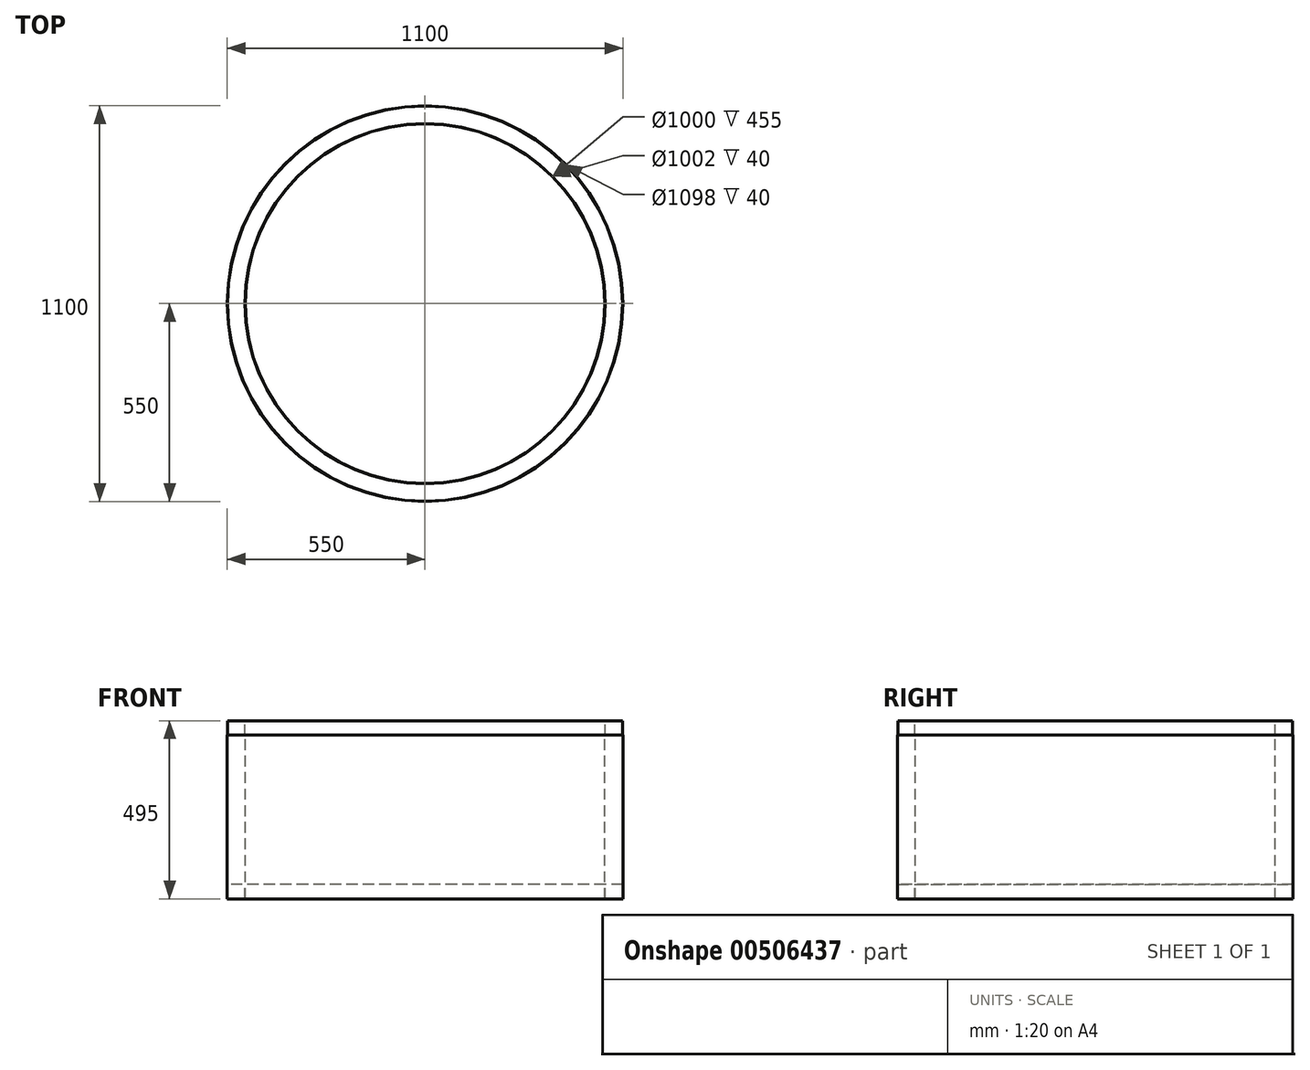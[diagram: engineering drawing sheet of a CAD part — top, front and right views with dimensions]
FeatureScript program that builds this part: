
annotation { "Feature Type Name" : "Feature", "Feature Type Description" : "" }
export const myFeature = defineFeature(function(context is Context, id is Id, definition is map)
    precondition{}
    {
        {
            var Q0;
            Q0=qCreatedBy(makeId("Front.planeOp"),FACE);
            var sketch = newSketch(context, id + "F0", { "sketchPlane" : qUnion([Q0])});
            skLineSegment(sketch, "E0", {"start": v(0, 150.29) * mm, "end": v(0, 1.7) * mm, "construction": true});
            skLineSegment(sketch, "E1", {"start": v(0, 450.26) * mm, "end": v(0, -453.52) * mm, "construction": true});
            skLineSegment(sketch, "E2", {"start": v(-500, -414.33) * mm, "end": v(-500, 40.67) * mm});
            skLineSegment(sketch, "E3", {"start": v(-500, 40.67) * mm, "end": v(-501, 40.67) * mm});
            skLineSegment(sketch, "E4", {"start": v(-501, 40.67) * mm, "end": v(-501, 80.67) * mm});
            skLineSegment(sketch, "E5", {"start": v(-501, 80.67) * mm, "end": v(-549, 80.67) * mm});
            skLineSegment(sketch, "E6", {"start": v(-549, 80.67) * mm, "end": v(-549, 40.67) * mm});
            skLineSegment(sketch, "E7", {"start": v(-549, 40.67) * mm, "end": v(-550, 40.67) * mm});
            skLineSegment(sketch, "E8", {"start": v(-550, 40.67) * mm, "end": v(-550, -414.33) * mm});
            skLineSegment(sketch, "E9", {"start": v(-550, -414.33) * mm, "end": v(-549, -414.33) * mm});
            skLineSegment(sketch, "E10", {"start": v(-549, -414.33) * mm, "end": v(-549, -374.33) * mm});
            skLineSegment(sketch, "E11", {"start": v(-549, -374.33) * mm, "end": v(-501, -374.33) * mm});
            skLineSegment(sketch, "E12", {"start": v(-501, -374.33) * mm, "end": v(-501, -414.33) * mm});
            skLineSegment(sketch, "E13", {"start": v(-501, -414.33) * mm, "end": v(-500, -414.33) * mm});
            skSolve(sketch);
        }
        {
            var Q0;
            Q0=qSketchRegion(id+"F0",true);
            var Q1;
            Q1=sQuery(id+"F0.wireOp",EDGE,"E1");
            revolve(context, id + "F1", {"entities" : qUnion([Q0]), "axis" : qUnion([Q1]), "revolveType" : RevolveType.FULL});
        }
    });
